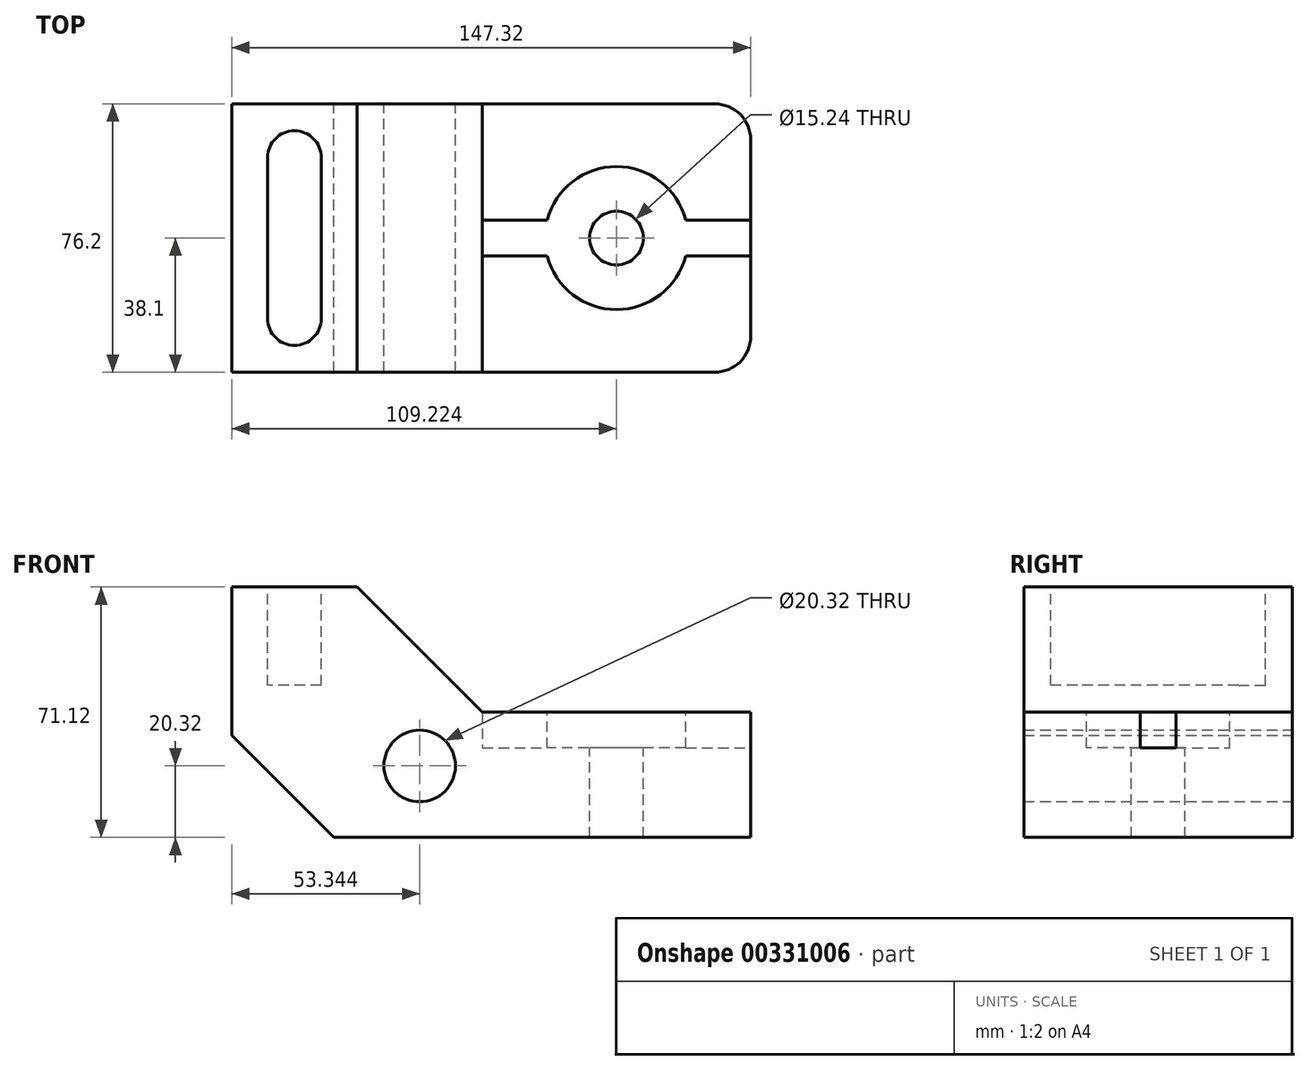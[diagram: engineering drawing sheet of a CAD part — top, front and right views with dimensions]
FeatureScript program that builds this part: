
annotation { "Feature Type Name" : "Feature", "Feature Type Description" : "" }
export const myFeature = defineFeature(function(context is Context, id is Id, definition is map)
    precondition{}
    {
        {
            var Q0;
            Q0=qCreatedBy(makeId("Front.planeOp"),FACE);
            var sketch = newSketch(context, id + "F0", { "sketchPlane" : qUnion([Q0])});
            skLineSegment(sketch, "E0", {"start": v(0, 0) * mm, "end": v(-28.96, 28.96) * mm});
            skLineSegment(sketch, "E1", {"start": v(-28.96, 28.96) * mm, "end": v(-28.96, 71.12) * mm});
            skLineSegment(sketch, "E2", {"start": v(-28.96, 71.12) * mm, "end": v(6.6, 71.12) * mm});
            skLineSegment(sketch, "E3", {"start": v(6.6, 71.12) * mm, "end": v(42.16, 35.56) * mm});
            skLineSegment(sketch, "E4", {"start": v(42.16, 35.56) * mm, "end": v(118.36, 35.56) * mm});
            skLineSegment(sketch, "E5", {"start": v(118.36, 35.56) * mm, "end": v(118.36, 0) * mm});
            skLineSegment(sketch, "E6", {"start": v(118.36, 0) * mm, "end": v(0, 0) * mm});
            skSolve(sketch);
        }
        {
            var Q0;
            Q0 = qSketchRegion(id + "F0", true);
            extrude(context, id + "F1", {"entities" : qUnion([Q0]), "depth" : 76.2 * mm});
        }
        {
            var Q0;
            Q0=makeQuery(id+"F1.opExtrude","SWEPT_FACE",FACE,{"disambiguationData":[OSD([sQuery(id+"F0.wireOp",EDGE,"E2")])]});
            var sketch = newSketch(context, id + "F2", { "sketchPlane" : qUnion([Q0])});
            skLineSegment(sketch, "E7", {"start": v(-18.8, -15.24) * mm, "end": v(-18.8, -60.96) * mm});
            skArc(sketch, "E8", {"start": v(-18.8, -15.24) * mm, "mid": v(-16.56, -9.85) * mm, "end": v(-11.18, -7.62) * mm});
            skArc(sketch, "E9", {"start": v(-18.8, -60.96) * mm, "mid": v(-16.56, -66.35) * mm, "end": v(-11.18, -68.58) * mm});
            skLineSegment(sketch, "E10", {"start": v(-11.18, 0) * mm, "end": v(-11.18, -76.2) * mm, "construction": true});
            skArc(sketch, "E11.MirrorCS", {"start": v(-3.56, -60.96) * mm, "mid": v(-5.79, -66.35) * mm, "end": v(-11.18, -68.58) * mm});
            skArc(sketch, "E12.MirrorCS", {"start": v(-3.56, -15.24) * mm, "mid": v(-5.79, -9.85) * mm, "end": v(-11.18, -7.62) * mm});
            skLineSegment(sketch, "E13.MirrorCS", {"start": v(-3.56, -15.24) * mm, "end": v(-3.56, -60.96) * mm});
            skSolve(sketch);
        }
        {
            var Q0;
            Q0 = qSketchRegion(id + "F2", true);
            extrude(context, id + "F3", {"entities" : qUnion([Q0]), "operationType" : NewBodyOperationType.REMOVE, "oppositeDirection" : true, "depth" : 27.94 * mm});
        }
        {
            var Q0;
            Q0=makeQuery(id+"F1.opExtrude","SWEPT_FACE",FACE,{"disambiguationData":[OSD([sQuery(id+"F0.wireOp",EDGE,"E4")])]});
            var sketch = newSketch(context, id + "F4", { "sketchPlane" : qUnion([Q0])});
            skPoint(sketch, "E14", {"position": v(80.26, -38.1) * mm});
            skPoint(sketch, "E14.positionSnap0", {"position": v(118.36, -38.1) * mm});
            skPoint(sketch, "E14.positionSnap1", {"position": v(80.26, 0) * mm});
            skSolve(sketch);
        }
        {
            var Q0;
            Q0=sQuery(id+"F4.wireOp",VERTEX,"E14");
            var Q1;
            Q1=makeQuery(id+"F1.opExtrude","SWEPT_BODY",BODY,{"disambiguationData":[OSD([sQuery(id+"F0.wireOp",EDGE,"E0"),sQuery(id+"F0.wireOp",EDGE,"E1"),sQuery(id+"F0.wireOp",EDGE,"E2"),sQuery(id+"F0.wireOp",EDGE,"E3"),sQuery(id+"F0.wireOp",EDGE,"E4"),sQuery(id+"F0.wireOp",EDGE,"E5"),sQuery(id+"F0.wireOp",EDGE,"E6")])]});
            hole(context, id + "F5", {"style" : HoleStyle.C_BORE, "endStyle" : HoleEndStyle.THROUGH, "holeDiameter" : 15.24 * mm, "cBoreDiameter" : 40.64 * mm, "cBoreDepth" : 10.16 * mm, "tappedDepth" : 12.7 * mm, "tapClearance" : 3, "locations" : qUnion([Q0]), "scope" : qUnion([Q1])});
        }
        {
            var Q0;
            Q0=makeQuery(id+"F1.opExtrude","SWEPT_FACE",FACE,{"disambiguationData":[OSD([sQuery(id+"F0.wireOp",EDGE,"E5")])]});
            var sketch = newSketch(context, id + "F6", { "sketchPlane" : qUnion([Q0])});
            skLineSegment(sketch, "E15.bottom", {"start": v(-43.18, 35.56) * mm, "end": v(-33.02, 35.56) * mm});
            skLineSegment(sketch, "E15.top", {"start": v(-43.18, 25.4) * mm, "end": v(-33.02, 25.4) * mm});
            skLineSegment(sketch, "E15.left", {"start": v(-43.18, 35.56) * mm, "end": v(-43.18, 25.4) * mm});
            skLineSegment(sketch, "E15.right", {"start": v(-33.02, 35.56) * mm, "end": v(-33.02, 25.4) * mm});
            skSolve(sketch);
        }
        {
            var Q0;
            Q0 = qSketchRegion(id + "F6", true);
            extrude(context, id + "F7", {"entities" : qUnion([Q0]), "operationType" : NewBodyOperationType.REMOVE, "oppositeDirection" : true, "depth" : 76.2 * mm});
        }
        {
            var Q0;
            Q0=makeQuery(id+"F1.opExtrude","CAP_FACE",FACE,{"disambiguationData":[OSD([sQuery(id+"F0.wireOp",EDGE,"E0"),sQuery(id+"F0.wireOp",EDGE,"E1"),sQuery(id+"F0.wireOp",EDGE,"E2"),sQuery(id+"F0.wireOp",EDGE,"E3"),sQuery(id+"F0.wireOp",EDGE,"E4"),sQuery(id+"F0.wireOp",EDGE,"E5"),sQuery(id+"F0.wireOp",EDGE,"E6")])],"isStart":true});
            var sketch = newSketch(context, id + "F8", { "sketchPlane" : qUnion([Q0])});
            skCircle(sketch, "E16", {"center": v(-24.38, 20.32) * mm, "radius": 10.16 * mm});
            skSolve(sketch);
        }
        {
            var Q0;
            Q0 = qSketchRegion(id + "F8", true);
            extrude(context, id + "F9", {"entities" : qUnion([Q0]), "operationType" : NewBodyOperationType.REMOVE, "endBound" : BoundingType.THROUGH_ALL, "oppositeDirection" : true, "depth" : 25.4 * mm});
        }
        {
            var Q0;
            Q0=makeQuery(id+"F1.opExtrude","CAP_EDGE",EDGE,{"disambiguationData":[OSD([sQuery(id+"F0.wireOp",EDGE,"E5")])],"isStart":false});
            var Q1;
            Q1=makeQuery(id+"F1.opExtrude","CAP_EDGE",EDGE,{"disambiguationData":[OSD([sQuery(id+"F0.wireOp",EDGE,"E5")])],"isStart":true});
            fillet(context, id + "F10", {"entities" : qUnion([Q0, Q1]), "radius" : 10.16 * mm, "tangentPropagation" : true, "allowEdgeOverflow" : false});
        }
    });
